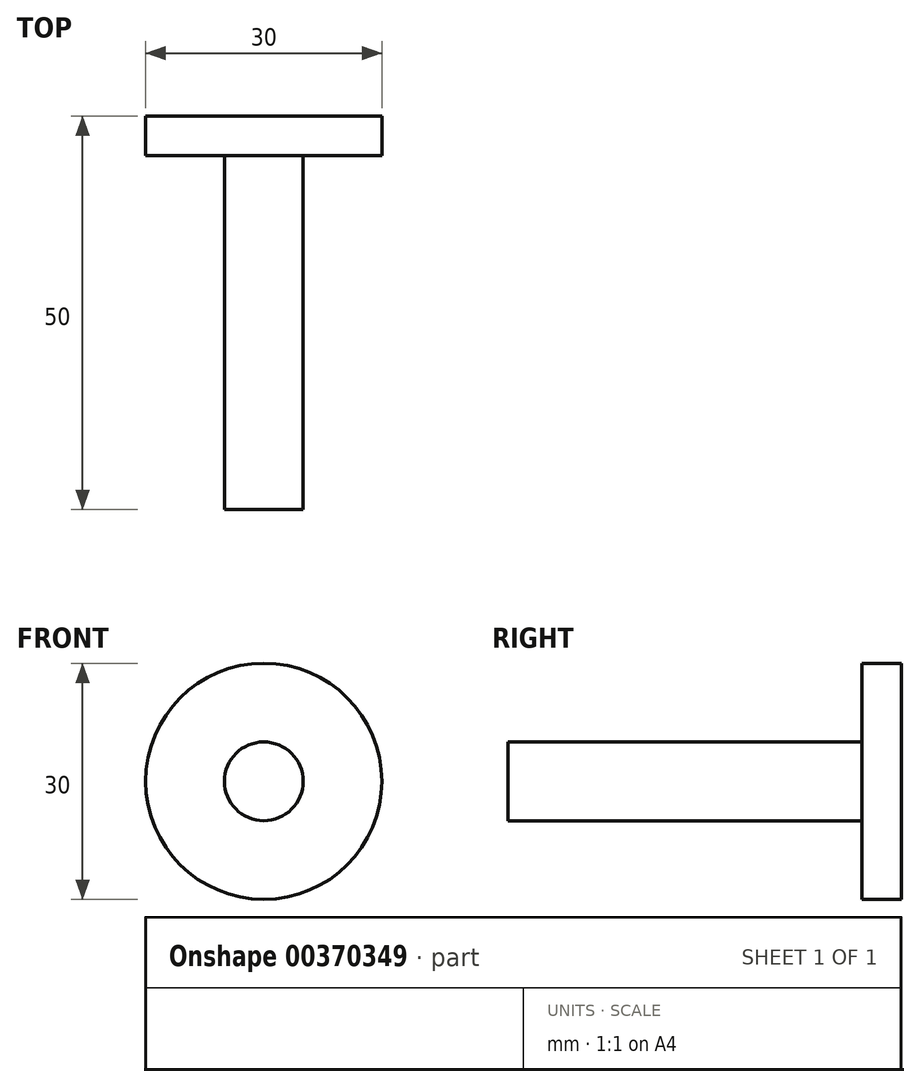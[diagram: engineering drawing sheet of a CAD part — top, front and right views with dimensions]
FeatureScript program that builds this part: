
annotation { "Feature Type Name" : "Feature", "Feature Type Description" : "" }
export const myFeature = defineFeature(function(context is Context, id is Id, definition is map)
    precondition{}
    {
        {
            var Q0;
            Q0=qCreatedBy(makeId("Right.planeOp"),FACE);
            var sketch = newSketch(context, id + "F0", { "sketchPlane" : qUnion([Q0])});
            skLineSegment(sketch, "E0", {"start": v(0, 0) * mm, "end": v(-45, 0) * mm});
            skLineSegment(sketch, "E1", {"start": v(-45, 0) * mm, "end": v(-45, 5) * mm});
            skLineSegment(sketch, "E2", {"start": v(-45, 5) * mm, "end": v(0, 5) * mm});
            skLineSegment(sketch, "E3", {"start": v(0, 5) * mm, "end": v(0, 15) * mm});
            skLineSegment(sketch, "E4", {"start": v(0, 15) * mm, "end": v(5, 15) * mm});
            skLineSegment(sketch, "E5", {"start": v(5, 15) * mm, "end": v(5, 0) * mm});
            skLineSegment(sketch, "E6", {"start": v(0, 0) * mm, "end": v(5, 0) * mm});
            skPoint(sketch, "E7.end.orphan", {"position": v(0, -10) * mm});
            skSolve(sketch);
        }
        {
            var Q0;
            Q0=makeQuery(id+"F0.imprint","IMPRINT",FACE,{"disambiguationData":[TD([[makeQuery(id+"F0.imprint","IMPRINT",EDGE,{"derivedFrom":sQuery(id+"F0.wireOp",EDGE,"E0")}),-1.0]])]});
            var Q1;
            Q1=sQuery(id+"F0.wireOp",EDGE,"E0");
            revolve(context, id + "F1", {"entities" : qUnion([Q0]), "axis" : qUnion([Q1]), "revolveType" : RevolveType.FULL});
        }
    });
